# Revit family: Gira_001330
name_source: partatom
category: Electrical Fixtures
revit_build: Autodesk Revit 2017 (Build: 20160225_1515(x64)
units: mm (PartAtom-declared; Revit-internal decimal feet)

## family parameters
Always vertical = Yes
Cut with Voids When Loaded = No
Maintain Annotation Orientation = No
Part Type = Normal
Room Calculation Point = No
Round Connector Dimension = Use Diameter
Shared = No
Work Plane-Based = No

## types (1)
- Connector WP SM grey
    BIM = https://media.live.bim.site
    BIMSITE_PRODUCT_ID = 0122b16c1ecfa36c0f6ed0cc1d6aa52c0234e6ab
    Colour = Grey
    Cost = 0 $
    Description = Connector WP SM GY Connector,grey Features: - For coupling several devices.
    GTIN = 4010337013303
    HAN = 001330
    HeinzeBIM = https://www.heinze.de
    Manufacturer = Gira
    Model = Coupling piece
    Suitable for built-up box flush-mounted switching equipment = No
    URL = https://www.gira.de

## geometry (parser evidence)
native form markers: Blend x2, Sweep x2
no freeform markers — native parametric forms only
